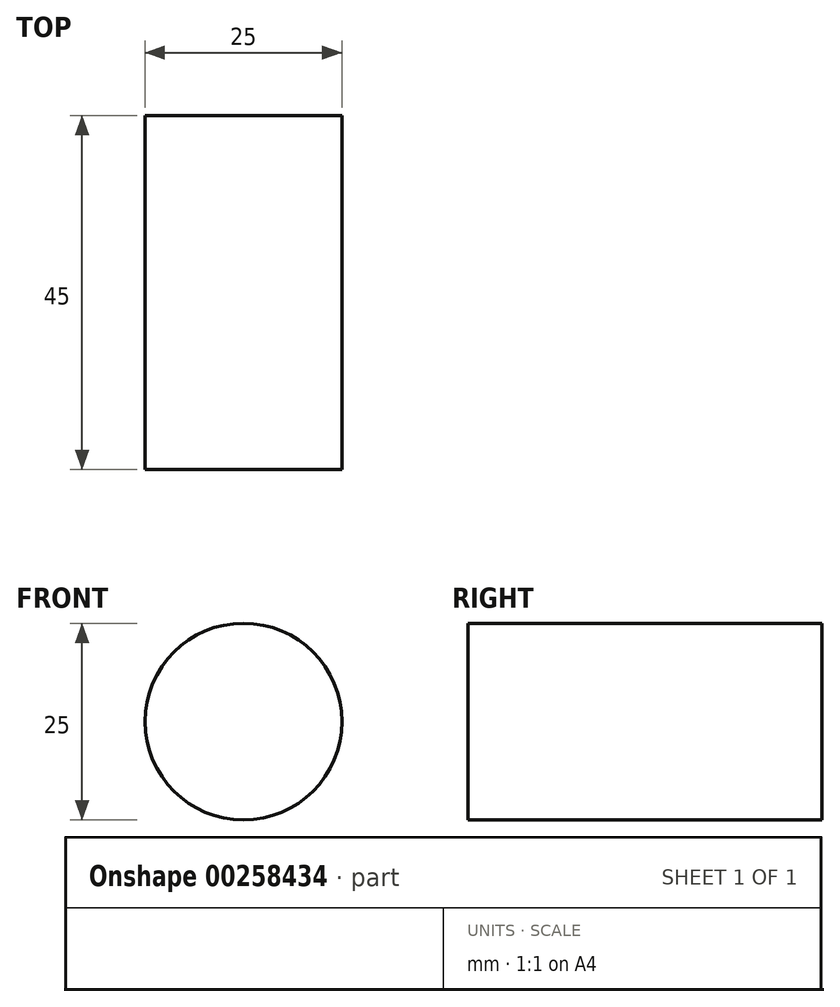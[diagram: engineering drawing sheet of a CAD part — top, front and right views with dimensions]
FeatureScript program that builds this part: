
annotation { "Feature Type Name" : "Feature", "Feature Type Description" : "" }
export const myFeature = defineFeature(function(context is Context, id is Id, definition is map)
    precondition{}
    {
        {
            var Q0;
            Q0=qCreatedBy(makeId("Front.planeOp"),FACE);
            var sketch = newSketch(context, id + "F0", { "sketchPlane" : qUnion([Q0])});
            skCircle(sketch, "E0", {"center": v(0, 0) * mm, "radius": 12.5 * mm});
            skSolve(sketch);
        }
        {
            var Q0;
            Q0 = qSketchRegion(id + "F0", true);
            extrude(context, id + "F1", {"entities" : qUnion([Q0]), "depth" : 45 * mm});
        }
    });
